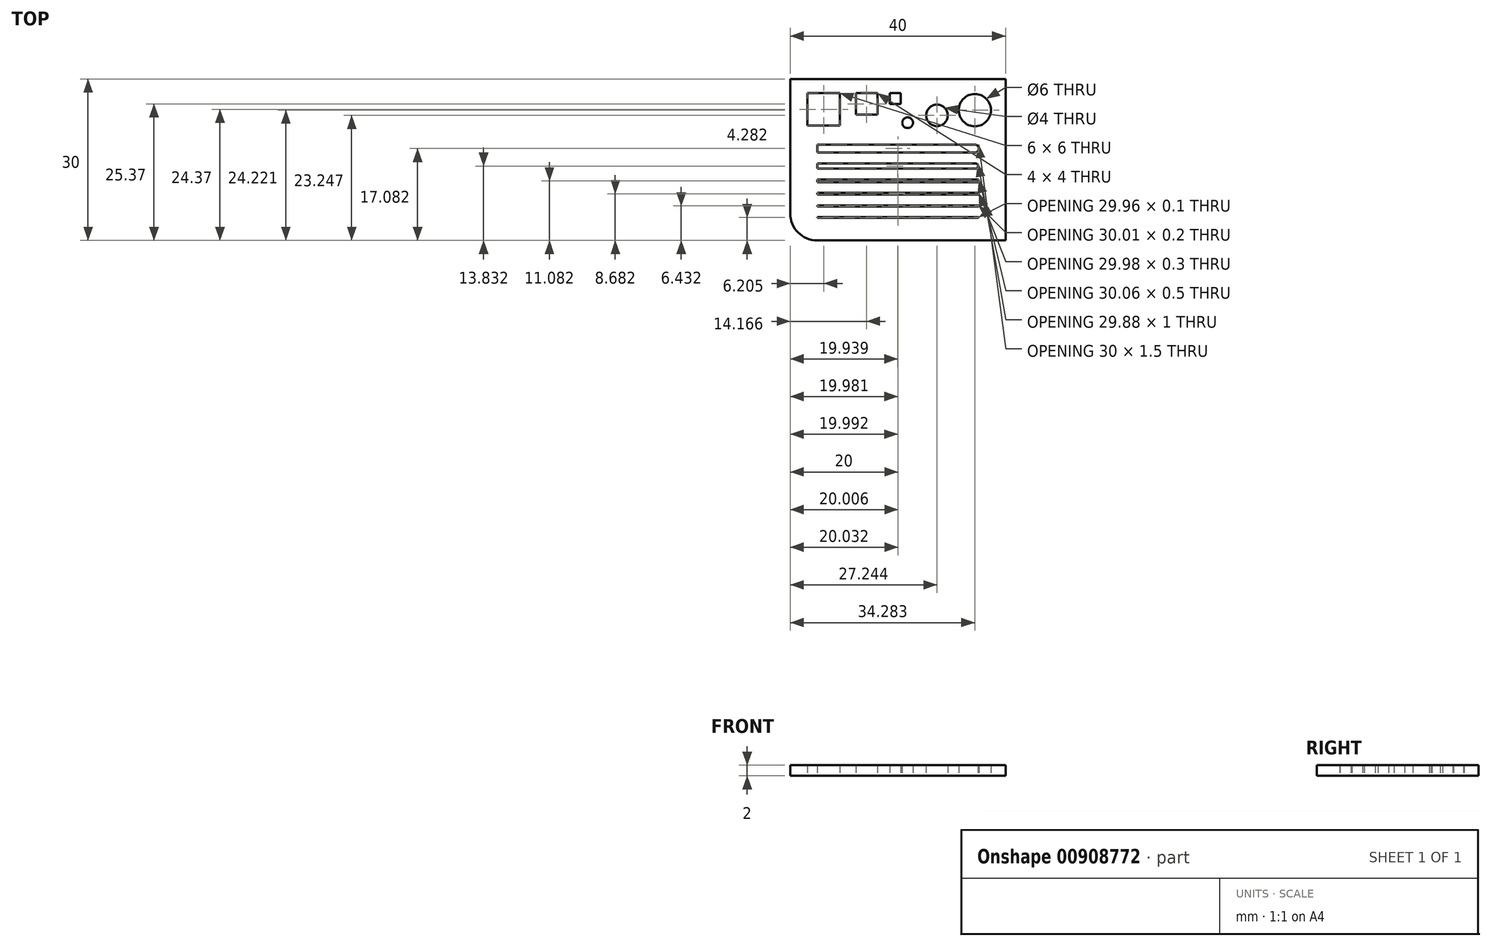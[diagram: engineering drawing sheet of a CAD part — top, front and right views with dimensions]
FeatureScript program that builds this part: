
annotation { "Feature Type Name" : "Feature", "Feature Type Description" : "" }
export const myFeature = defineFeature(function(context is Context, id is Id, definition is map)
    precondition{}
    {
        {
            var Q0;
            Q0=qCreatedBy(makeId("Top.planeOp"),FACE);
            var sketch = newSketch(context, id + "F0", { "sketchPlane" : qUnion([Q0])});
            skLineSegment(sketch, "E0.bottom", {"start": v(5, 0) * mm, "end": v(40, 0) * mm});
            skLineSegment(sketch, "E0.top", {"start": v(0, 30) * mm, "end": v(40, 30) * mm});
            skLineSegment(sketch, "E0.left", {"start": v(0, 5) * mm, "end": v(0, 30) * mm});
            skLineSegment(sketch, "E0.right", {"start": v(40, 0) * mm, "end": v(40, 30) * mm});
            skLineSegment(sketch, "E1.bottom", {"start": v(3.2, 27.37) * mm, "end": v(9.2, 27.37) * mm});
            skLineSegment(sketch, "E1.top", {"start": v(3.2, 21.37) * mm, "end": v(9.2, 21.37) * mm});
            skLineSegment(sketch, "E1.left", {"start": v(3.2, 27.37) * mm, "end": v(3.2, 21.37) * mm});
            skLineSegment(sketch, "E1.right", {"start": v(9.2, 27.37) * mm, "end": v(9.2, 21.37) * mm});
            skLineSegment(sketch, "E2.bottom", {"start": v(12.17, 27.37) * mm, "end": v(16.17, 27.37) * mm});
            skLineSegment(sketch, "E2.top", {"start": v(12.17, 23.37) * mm, "end": v(16.17, 23.37) * mm});
            skLineSegment(sketch, "E2.left", {"start": v(12.17, 27.37) * mm, "end": v(12.17, 23.37) * mm});
            skLineSegment(sketch, "E2.right", {"start": v(16.17, 27.37) * mm, "end": v(16.17, 23.37) * mm});
            skLineSegment(sketch, "E3.bottom", {"start": v(18.51, 27.37) * mm, "end": v(20.51, 27.37) * mm});
            skLineSegment(sketch, "E3.top", {"start": v(18.51, 25.37) * mm, "end": v(20.51, 25.37) * mm});
            skLineSegment(sketch, "E3.left", {"start": v(18.51, 27.37) * mm, "end": v(18.51, 25.37) * mm});
            skLineSegment(sketch, "E3.right", {"start": v(20.51, 27.37) * mm, "end": v(20.51, 25.37) * mm});
            skCircle(sketch, "E4", {"center": v(34.28, 24.22) * mm, "radius": 3 * mm});
            skCircle(sketch, "E5", {"center": v(27.24, 23.25) * mm, "radius": 2 * mm});
            skCircle(sketch, "E6", {"center": v(21.8, 21.89) * mm, "radius": 1 * mm});
            skPoint(sketch, "E7.visualSharp", {"position": v(0, 0) * mm});
            skArc(sketch, "E7.filletArc", {"start": v(0, 5) * mm, "mid": v(1.46, 1.46) * mm, "end": v(5, 0) * mm});
            skLineSegment(sketch, "E8.bottom", {"start": v(5, 17.83) * mm, "end": v(34.25, 17.83) * mm});
            skLineSegment(sketch, "E8.top", {"start": v(5, 16.33) * mm, "end": v(34.25, 16.33) * mm});
            skLineSegment(sketch, "E8.left", {"start": v(5, 17.83) * mm, "end": v(5, 16.33) * mm});
            skLineSegment(sketch, "E8.right", {"start": v(35, 17.08) * mm, "end": v(35, 17.08) * mm});
            skLineSegment(sketch, "E9.bottom", {"start": v(5, 14.33) * mm, "end": v(34.38, 14.33) * mm});
            skLineSegment(sketch, "E9.top", {"start": v(5, 13.33) * mm, "end": v(34.38, 13.33) * mm});
            skLineSegment(sketch, "E9.left", {"start": v(5, 14.33) * mm, "end": v(5, 13.33) * mm});
            skLineSegment(sketch, "E9.right", {"start": v(34.88, 13.83) * mm, "end": v(34.88, 13.83) * mm});
            skLineSegment(sketch, "E10.bottom", {"start": v(5, 11.33) * mm, "end": v(34.81, 11.33) * mm});
            skLineSegment(sketch, "E10.top", {"start": v(5, 10.83) * mm, "end": v(34.81, 10.83) * mm});
            skLineSegment(sketch, "E10.left", {"start": v(5, 11.33) * mm, "end": v(5, 10.83) * mm});
            skLineSegment(sketch, "E10.right", {"start": v(35.06, 11.08) * mm, "end": v(35.06, 11.08) * mm});
            skLineSegment(sketch, "E11.bottom", {"start": v(5, 8.83) * mm, "end": v(34.83, 8.83) * mm});
            skLineSegment(sketch, "E11.top", {"start": v(5, 8.53) * mm, "end": v(34.83, 8.53) * mm});
            skLineSegment(sketch, "E11.left", {"start": v(5, 8.83) * mm, "end": v(5, 8.53) * mm});
            skLineSegment(sketch, "E11.right", {"start": v(34.98, 8.68) * mm, "end": v(34.98, 8.68) * mm});
            skLineSegment(sketch, "E12.bottom", {"start": v(5, 6.53) * mm, "end": v(34.91, 6.53) * mm});
            skLineSegment(sketch, "E12.top", {"start": v(5, 6.33) * mm, "end": v(34.91, 6.33) * mm});
            skLineSegment(sketch, "E12.left", {"start": v(5, 6.53) * mm, "end": v(5, 6.33) * mm});
            skLineSegment(sketch, "E12.right", {"start": v(35.01, 6.43) * mm, "end": v(35.01, 6.43) * mm});
            skLineSegment(sketch, "E13.bottom", {"start": v(5, 4.33) * mm, "end": v(34.91, 4.33) * mm});
            skLineSegment(sketch, "E13.top", {"start": v(5, 4.23) * mm, "end": v(34.91, 4.23) * mm});
            skLineSegment(sketch, "E13.left", {"start": v(5, 4.33) * mm, "end": v(5, 4.23) * mm});
            skLineSegment(sketch, "E13.right", {"start": v(34.96, 4.28) * mm, "end": v(34.96, 4.28) * mm});
            skPoint(sketch, "E14.visualSharp", {"position": v(35, 17.83) * mm});
            skArc(sketch, "E14.filletArc", {"start": v(35, 17.08) * mm, "mid": v(34.78, 17.61) * mm, "end": v(34.25, 17.83) * mm});
            skPoint(sketch, "E15.visualSharp", {"position": v(35, 16.33) * mm});
            skArc(sketch, "E15.filletArc", {"start": v(34.25, 16.33) * mm, "mid": v(34.78, 16.55) * mm, "end": v(35, 17.08) * mm});
            skPoint(sketch, "E16.visualSharp", {"position": v(34.88, 14.33) * mm});
            skArc(sketch, "E16.filletArc", {"start": v(34.88, 13.83) * mm, "mid": v(34.73, 14.19) * mm, "end": v(34.38, 14.33) * mm});
            skPoint(sketch, "E17.visualSharp", {"position": v(34.88, 13.33) * mm});
            skArc(sketch, "E17.filletArc", {"start": v(34.38, 13.33) * mm, "mid": v(34.73, 13.48) * mm, "end": v(34.88, 13.83) * mm});
            skPoint(sketch, "E18.visualSharp", {"position": v(35.06, 11.33) * mm});
            skArc(sketch, "E18.filletArc", {"start": v(35.06, 11.08) * mm, "mid": v(35, 11.26) * mm, "end": v(34.81, 11.33) * mm});
            skPoint(sketch, "E19.visualSharp", {"position": v(35.06, 10.83) * mm});
            skArc(sketch, "E19.filletArc", {"start": v(34.81, 10.83) * mm, "mid": v(35, 10.9) * mm, "end": v(35.06, 11.08) * mm});
            skPoint(sketch, "E20.visualSharp", {"position": v(34.98, 8.83) * mm});
            skArc(sketch, "E20.filletArc", {"start": v(34.98, 8.68) * mm, "mid": v(34.94, 8.79) * mm, "end": v(34.83, 8.83) * mm});
            skPoint(sketch, "E21.visualSharp", {"position": v(34.98, 8.53) * mm});
            skArc(sketch, "E21.filletArc", {"start": v(34.83, 8.53) * mm, "mid": v(34.94, 8.58) * mm, "end": v(34.98, 8.68) * mm});
            skPoint(sketch, "E22.visualSharp", {"position": v(35.01, 6.53) * mm});
            skArc(sketch, "E22.filletArc", {"start": v(35.01, 6.43) * mm, "mid": v(34.98, 6.5) * mm, "end": v(34.91, 6.53) * mm});
            skPoint(sketch, "E23.visualSharp", {"position": v(35.01, 6.33) * mm});
            skArc(sketch, "E23.filletArc", {"start": v(34.91, 6.33) * mm, "mid": v(34.98, 6.36) * mm, "end": v(35.01, 6.43) * mm});
            skPoint(sketch, "E24.visualSharp", {"position": v(34.96, 4.33) * mm});
            skArc(sketch, "E24.filletArc", {"start": v(34.96, 4.28) * mm, "mid": v(34.95, 4.32) * mm, "end": v(34.91, 4.33) * mm});
            skPoint(sketch, "E25.visualSharp", {"position": v(34.96, 4.23) * mm});
            skArc(sketch, "E25.filletArc", {"start": v(34.91, 4.23) * mm, "mid": v(34.95, 4.25) * mm, "end": v(34.96, 4.28) * mm});
            skSolve(sketch);
        }
        {
            var Q0;
            Q0=makeQuery(id+"F0.imprint","IMPRINT",FACE,{"disambiguationData":[TD([[makeQuery(id+"F0.imprint","IMPRINT",EDGE,{"derivedFrom":sQuery(id+"F0.wireOp",EDGE,"E0.bottom")}),1.0]])]});
            extrude(context, id + "F1", {"entities" : qUnion([Q0]), "depth" : 2 * mm, "offsetDistance" : 25 * mm});
        }
    });
